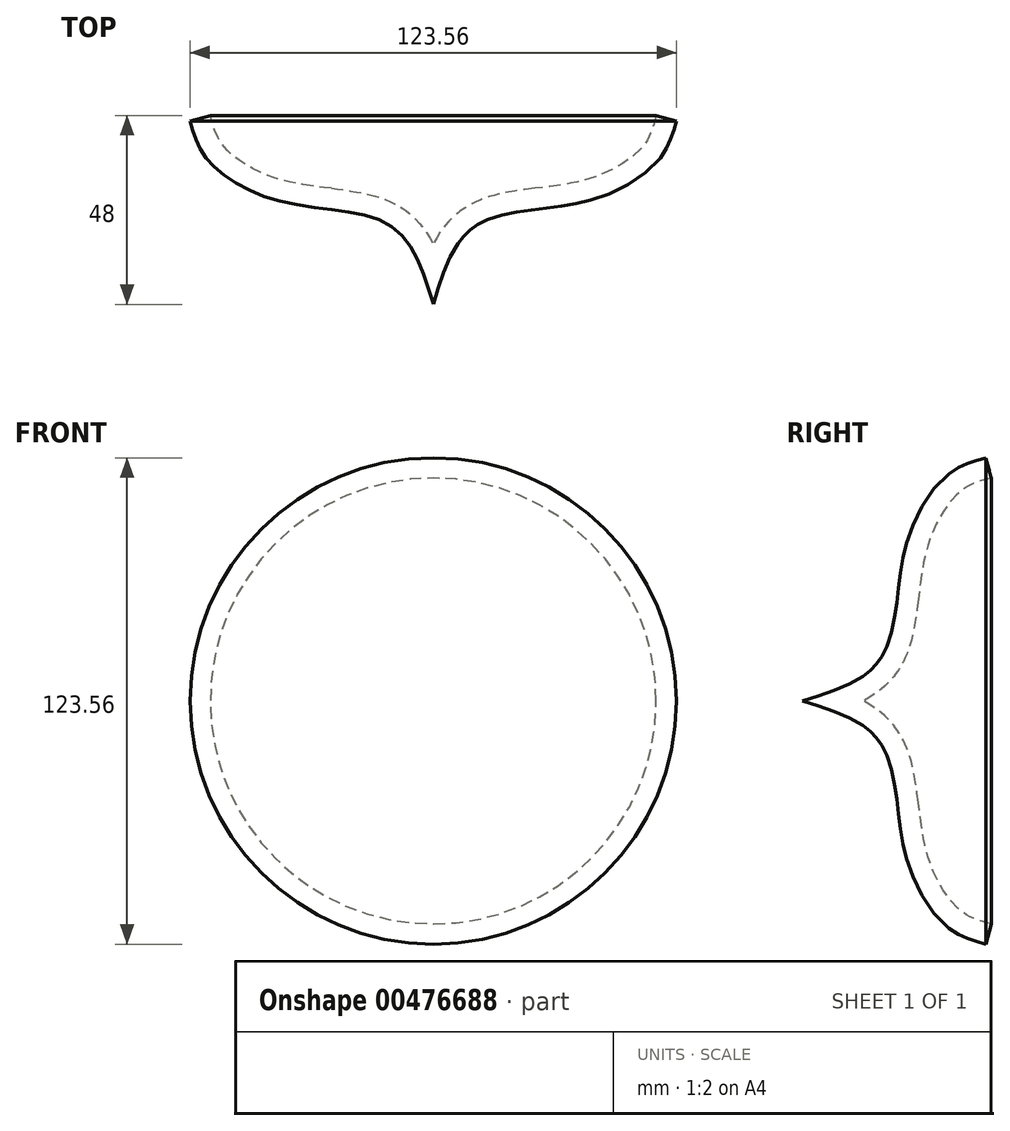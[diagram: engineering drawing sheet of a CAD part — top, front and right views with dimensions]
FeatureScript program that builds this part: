
annotation { "Feature Type Name" : "Feature", "Feature Type Description" : "" }
export const myFeature = defineFeature(function(context is Context, id is Id, definition is map)
    precondition{}
    {
        {
            var Q0;
            Q0=qCreatedBy(makeId("Top.planeOp"),FACE);
            var sketch = newSketch(context, id + "F0", { "sketchPlane" : qUnion([Q0])});
            skFitSpline(sketch, "E0", {"points": [v(-61.78, 20.6) * mm, v(-57.4, 10.8) * mm, v(-38.15, 0) * mm, v(-10.8, -6.08) * mm, v(0, -26) * mm], "startDerivative": vector(14.98, -54.67) * mm, "endDerivative": vector(27.2, -90.68) * mm});
            skFitSpline(sketch, "E1.0", {"points": [v(-56.64, 22) * mm, v(-56.32, 20.86) * mm, v(-55.9, 19.3) * mm, v(-55.23, 17.5) * mm, v(-54.66, 16.26) * mm, v(-54.09, 15.3) * mm, v(-53.54, 14.53) * mm, v(-52.93, 13.76) * mm, v(-51.98, 12.75) * mm, v(-50.54, 11.5) * mm, v(-48.84, 10.25) * mm, v(-46.9, 9.05) * mm, v(-44.76, 7.93) * mm, v(-42.43, 6.9) * mm, v(-40.36, 6.16) * mm, v(-38.64, 5.63) * mm, v(-37.33, 5.28) * mm, v(-35.98, 4.97) * mm, v(-34.58, 4.7) * mm, v(-33.13, 4.44) * mm, v(-31.14, 4.14) * mm, v(-28.58, 3.8) * mm, v(-25.4, 3.41) * mm, v(-22.2, 2.99) * mm, v(-18.96, 2.46) * mm, v(-15.75, 1.76) * mm, v(-13.1, 0.95) * mm, v(-11.03, 0.11) * mm, v(-9.76, -0.5) * mm, v(-8.75, -1.07) * mm, v(-8.01, -1.52) * mm, v(-7.3, -2.01) * mm, v(-6.37, -2.7) * mm, v(-5.28, -3.62) * mm, v(-3.7, -5.2) * mm, v(-1.98, -7.32) * mm, v(-0.3, -10.05) * mm, v(1.58, -13.82) * mm, v(3.38, -18.7) * mm, v(4.54, -22.57) * mm, v(5.1, -24.46) * mm]});
            skLineSegment(sketch, "E2", {"start": v(0, -26) * mm, "end": v(0, -10.7) * mm});
            skLineSegment(sketch, "E3", {"start": v(-61.78, 20.6) * mm, "end": v(-56.64, 22) * mm});
            skFitSpline(sketch, "E4", {"points": [v(-25.89, 3.47) * mm, v(-16.57, 7.37) * mm, v(-8.93, 19.07) * mm, v(-5.35, 38.17) * mm, v(-5.35, 48.9) * mm], "startDerivative": vector(45.12, 12.45) * mm, "endDerivative": vector(-1.79, 43.6) * mm});
            skLineSegment(sketch, "E5", {"start": v(-5.35, 48.9) * mm, "end": v(0, 48.9) * mm});
            skLineSegment(sketch, "E6", {"start": v(0, 48.9) * mm, "end": v(0, -10.7) * mm});
            skLineSegment(sketch, "E7.bottom", {"start": v(-17.97, 44.2) * mm, "end": v(-5.2, 44.2) * mm});
            skLineSegment(sketch, "E7.top", {"start": v(-17.97, 42.36) * mm, "end": v(-5.2, 42.36) * mm});
            skLineSegment(sketch, "E7.left", {"start": v(-17.97, 44.2) * mm, "end": v(-17.97, 42.36) * mm});
            skLineSegment(sketch, "E8.bottom", {"start": v(-18.04, 40.66) * mm, "end": v(-5.23, 40.66) * mm});
            skLineSegment(sketch, "E8.top", {"start": v(-18.04, 39.02) * mm, "end": v(-5.3, 39.02) * mm});
            skLineSegment(sketch, "E8.left", {"start": v(-18.04, 40.66) * mm, "end": v(-18.04, 39.02) * mm});
            skLineSegment(sketch, "E9.bottom", {"start": v(-18.11, 37.46) * mm, "end": v(-5.4, 37.46) * mm});
            skLineSegment(sketch, "E9.top", {"start": v(-18.11, 36.04) * mm, "end": v(-5.51, 36.04) * mm});
            skLineSegment(sketch, "E9.left", {"start": v(-18.11, 37.46) * mm, "end": v(-18.11, 36.04) * mm});
            skSolve(sketch);
        }
        {
            var Q0;
            Q0=makeQuery(id+"F0.imprint","IMPRINT",FACE,{"disambiguationData":[TD([[makeQuery(id+"F0.imprint","IMPRINT",EDGE,{"derivedFrom":sQuery(id+"F0.wireOp",EDGE,"E0")}),1.0]])]});
            var Q1;
            Q1=sQuery(id+"F0.wireOp",EDGE,"E6");
            revolve(context, id + "F1", {"entities" : qUnion([Q0]), "axis" : qUnion([Q1]), "revolveType" : RevolveType.FULL});
        }
    });
